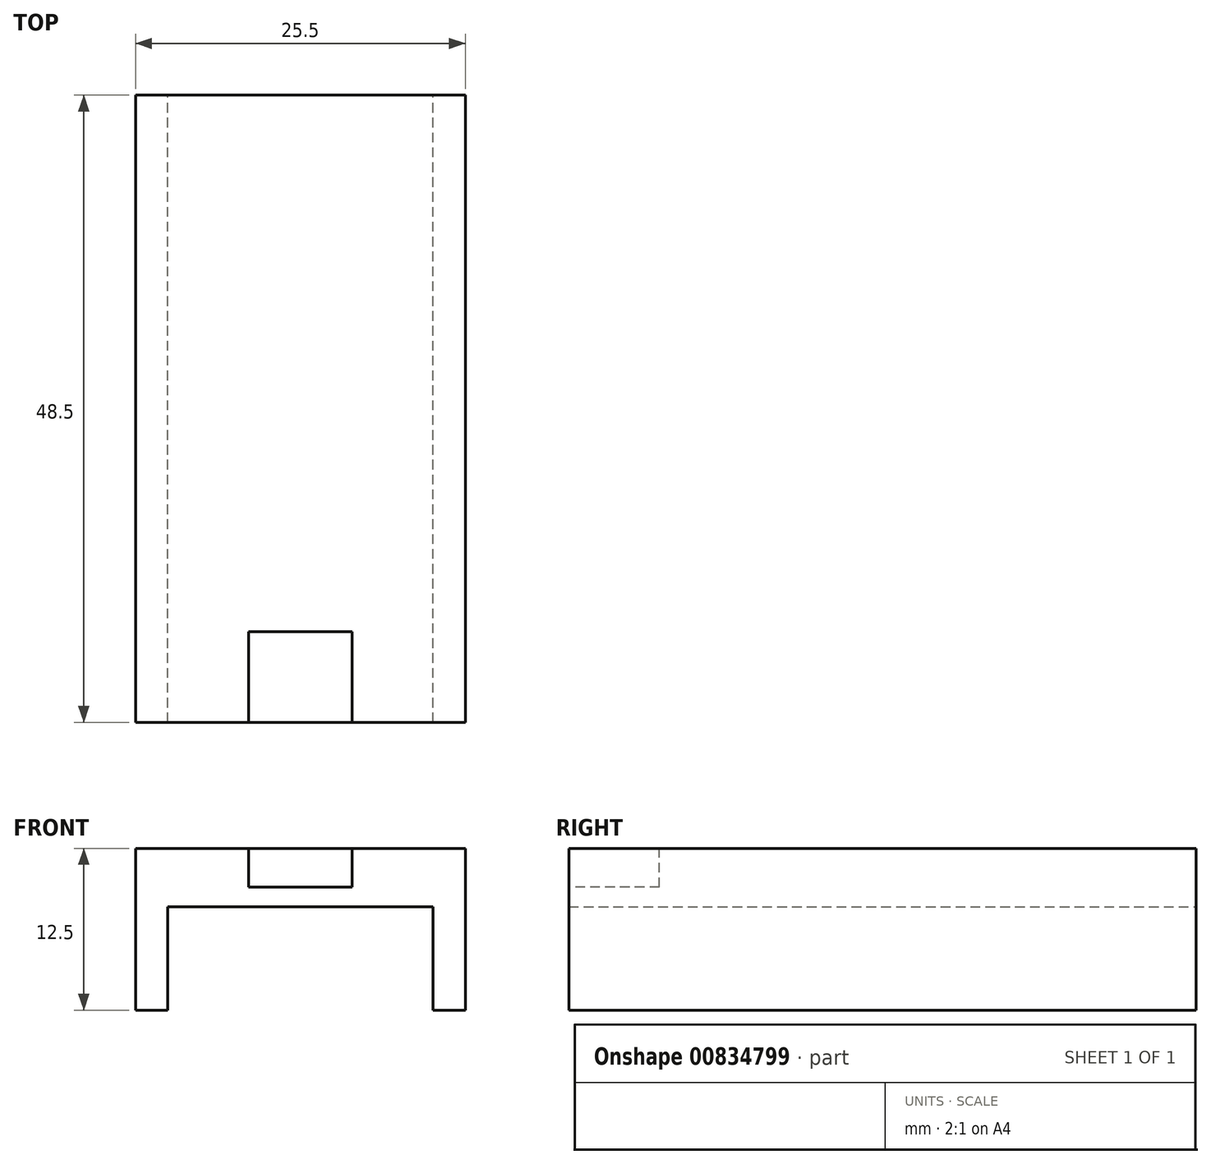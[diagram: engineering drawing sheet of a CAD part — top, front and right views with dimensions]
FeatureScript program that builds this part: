
annotation { "Feature Type Name" : "Feature", "Feature Type Description" : "" }
export const myFeature = defineFeature(function(context is Context, id is Id, definition is map)
    precondition{}
    {
        {
            var Q0;
            Q0=qCreatedBy(makeId("Front.planeOp"),FACE);
            var sketch = newSketch(context, id + "F0", { "sketchPlane" : qUnion([Q0])});
            skLineSegment(sketch, "E0.bottom", {"start": v(-12.75, 8) * mm, "end": v(12.75, 8) * mm});
            skLineSegment(sketch, "E0.top", {"start": v(-12.75, 12.5) * mm, "end": v(12.75, 12.5) * mm});
            skLineSegment(sketch, "E0.left", {"start": v(-12.75, 8) * mm, "end": v(-12.75, 12.5) * mm});
            skLineSegment(sketch, "E0.right", {"start": v(12.75, 8) * mm, "end": v(12.75, 12.5) * mm});
            skPoint(sketch, "E1", {"position": v(0, 12.5) * mm});
            skLineSegment(sketch, "E2.bottom", {"start": v(12.75, 8) * mm, "end": v(10.25, 8) * mm});
            skLineSegment(sketch, "E2.top", {"start": v(12.75, 0) * mm, "end": v(10.25, 0) * mm});
            skLineSegment(sketch, "E2.left", {"start": v(12.75, 8) * mm, "end": v(12.75, 0) * mm});
            skLineSegment(sketch, "E2.right", {"start": v(10.25, 8) * mm, "end": v(10.25, 0) * mm});
            skLineSegment(sketch, "E3.bottom", {"start": v(-12.75, 8) * mm, "end": v(-10.25, 8) * mm});
            skLineSegment(sketch, "E3.top", {"start": v(-12.75, 0) * mm, "end": v(-10.25, 0) * mm});
            skLineSegment(sketch, "E3.left", {"start": v(-12.75, 8) * mm, "end": v(-12.75, 0) * mm});
            skLineSegment(sketch, "E3.right", {"start": v(-10.25, 8) * mm, "end": v(-10.25, 0) * mm});
            skSolve(sketch);
        }
        {
            var Q0;
            Q0 = qSketchRegion(id + "F0", true);
            extrude(context, id + "F1", {"entities" : qUnion([Q0]), "endBound" : BoundingType.SYMMETRIC, "depth" : 48.5 * mm, "offsetDistance" : 25 * mm});
        }
        {
            var Q0;
            Q0=makeQuery(id+"F1.opExtrude","CAP_FACE",FACE,{"disambiguationData":[OSD([sQuery(id+"F0.wireOp",EDGE,"E0.bottom"),sQuery(id+"F0.wireOp",EDGE,"E0.top"),sQuery(id+"F0.wireOp",EDGE,"E0.left"),sQuery(id+"F0.wireOp",EDGE,"E0.right"),sQuery(id+"F0.wireOp",EDGE,"E2.top"),sQuery(id+"F0.wireOp",EDGE,"E2.left"),sQuery(id+"F0.wireOp",EDGE,"E2.right"),sQuery(id+"F0.wireOp",EDGE,"E3.top"),sQuery(id+"F0.wireOp",EDGE,"E3.left"),sQuery(id+"F0.wireOp",EDGE,"E3.right")])],"isStart":false});
            var sketch = newSketch(context, id + "F2", { "sketchPlane" : qUnion([Q0])});
            skLineSegment(sketch, "E4.bottom", {"start": v(-4, 9.5) * mm, "end": v(4, 9.5) * mm});
            skLineSegment(sketch, "E4.top", {"start": v(-4, 12.5) * mm, "end": v(4, 12.5) * mm});
            skLineSegment(sketch, "E4.left", {"start": v(-4, 9.5) * mm, "end": v(-4, 12.5) * mm});
            skLineSegment(sketch, "E4.right", {"start": v(4, 9.5) * mm, "end": v(4, 12.5) * mm});
            skPoint(sketch, "E5", {"position": v(0, 9.5) * mm});
            skSolve(sketch);
        }
        {
            var Q0;
            Q0 = qSketchRegion(id + "F2", true);
            extrude(context, id + "F3", {"entities" : qUnion([Q0]), "operationType" : NewBodyOperationType.REMOVE, "oppositeDirection" : true, "depth" : 7 * mm, "offsetDistance" : 25 * mm});
        }
    });
